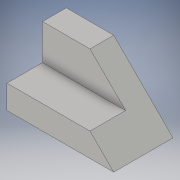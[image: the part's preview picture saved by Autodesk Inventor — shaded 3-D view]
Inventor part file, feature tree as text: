
AUTODESK INVENTOR PART (.ipt)
format: ipt  version: 2016 (Build 200138000, 138)  size: 112,128 bytes
history: native  units: in
note: dims shown in document units (in); Inventor stores cm internally (conversion verified against a paired STEP export)
features: extrude x4, sketch x4
ambient origin geometry x8: Origin, YZ Plane, XZ Plane, XY Plane, X Axis, Y Axis, Z Axis, Center Point
bodies: Solid1 (feature_tree)
feature tree (8):
  extrude  "Extrusion1"  Depth=1.25in
  extrude  "Extrusion2"  Depth=0.75in
  extrude  "Extrusion3"  Depth=0.75in TaperAngle=0.0deg
  extrude  "Extrusion4"  Depth=0.75in TaperAngle=0.0deg
  sketch  "Sketch1"  dims[d0=2.25in d1=1.25in]
  sketch  "Sketch2"  dims[d2=1.25in d3=0.0in d4=0.75in]
  sketch  "Sketch3"  dims[d5=2.25in d6=0.75in d7=0.0in]
  sketch  "Sketch4"  dims[d8=1.75in d9=0.75in d10=0.0in d11=1.0in d12=0.75in d13=0.0in]
